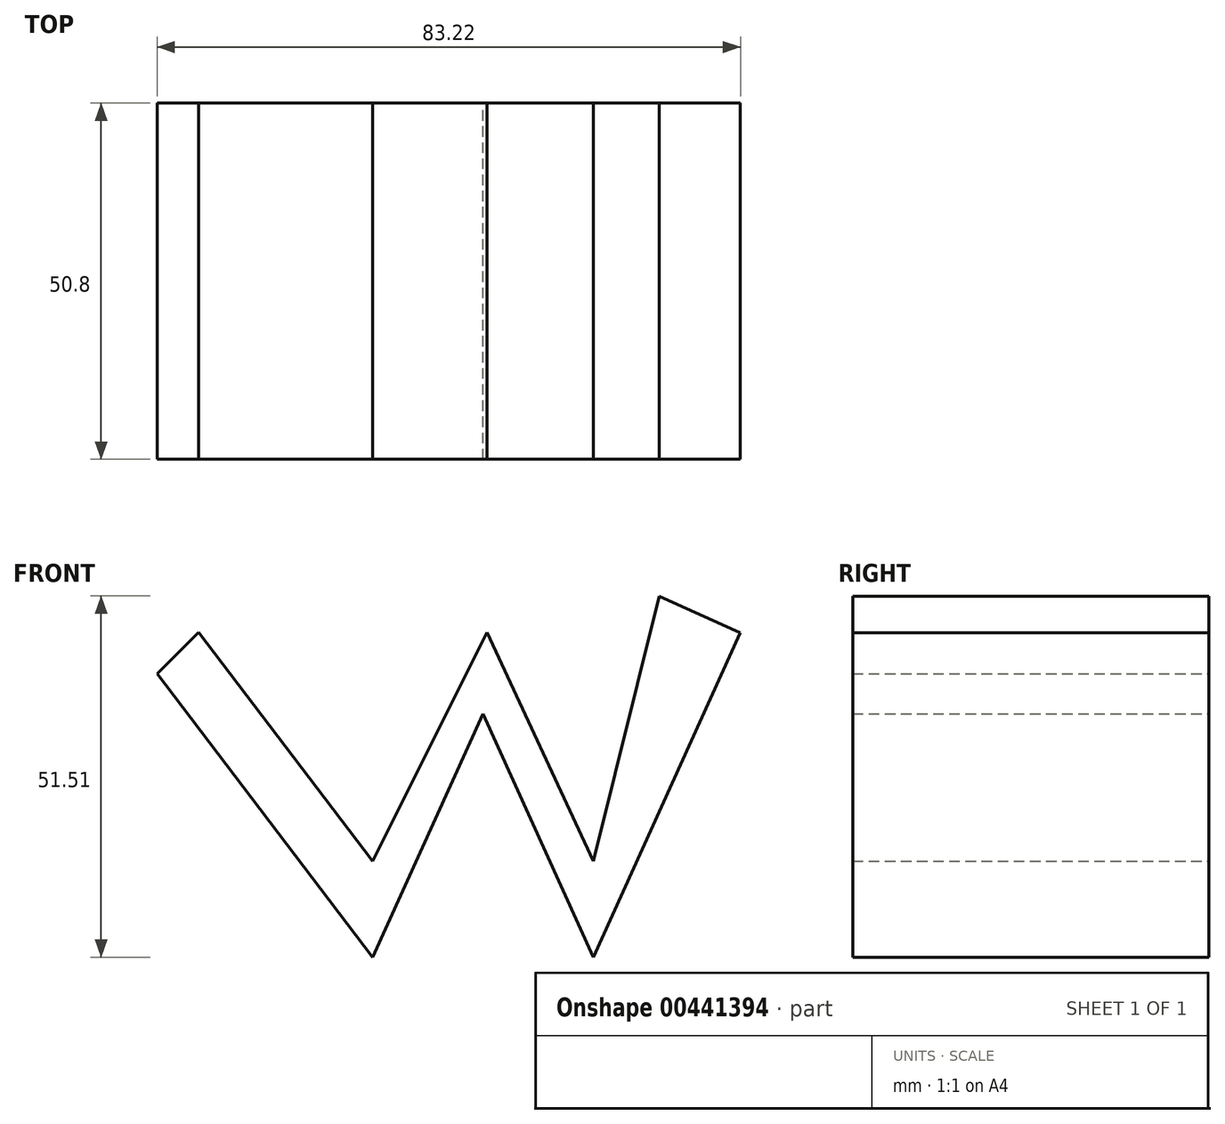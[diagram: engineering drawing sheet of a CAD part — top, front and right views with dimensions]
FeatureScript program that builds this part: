
annotation { "Feature Type Name" : "Feature", "Feature Type Description" : "" }
export const myFeature = defineFeature(function(context is Context, id is Id, definition is map)
    precondition{}
    {
        {
            var Q0;
            Q0=qCreatedBy(makeId("Front.planeOp"),FACE);
            var sketch = newSketch(context, id + "F0", { "sketchPlane" : qUnion([Q0])});
            skLineSegment(sketch, "E0", {"start": v(-62.23, 36.04) * mm, "end": v(-31.48, -4.4) * mm});
            skLineSegment(sketch, "E1", {"start": v(-31.48, -4.4) * mm, "end": v(-15.74, 30.3) * mm});
            skLineSegment(sketch, "E2", {"start": v(-15.74, 30.3) * mm, "end": v(0, -4.4) * mm});
            skLineSegment(sketch, "E3", {"start": v(0, -4.4) * mm, "end": v(20.99, 41.87) * mm});
            skLineSegment(sketch, "E4", {"start": v(20.99, 41.87) * mm, "end": v(9.42, 47.12) * mm});
            skLineSegment(sketch, "E5", {"start": v(9.42, 47.12) * mm, "end": v(0, 9.3) * mm});
            skLineSegment(sketch, "E6", {"start": v(0, 9.3) * mm, "end": v(-15.19, 41.93) * mm});
            skLineSegment(sketch, "E7", {"start": v(-15.19, 41.93) * mm, "end": v(-31.48, 9.3) * mm});
            skLineSegment(sketch, "E8", {"start": v(-31.48, 9.3) * mm, "end": v(-56.3, 41.93) * mm});
            skLineSegment(sketch, "E9", {"start": v(-56.3, 41.93) * mm, "end": v(-62.23, 36.04) * mm});
            skSolve(sketch);
        }
        {
            var Q0;
            Q0=makeQuery(id+"F0.imprint","IMPRINT",FACE,{"disambiguationData":[TD([[makeQuery(id+"F0.imprint","IMPRINT",EDGE,{"derivedFrom":sQuery(id+"F0.wireOp",EDGE,"E0")}),1.0]])]});
            extrude(context, id + "F1", {"entities" : qUnion([Q0]), "depth" : 50.8 * mm});
        }
    });
